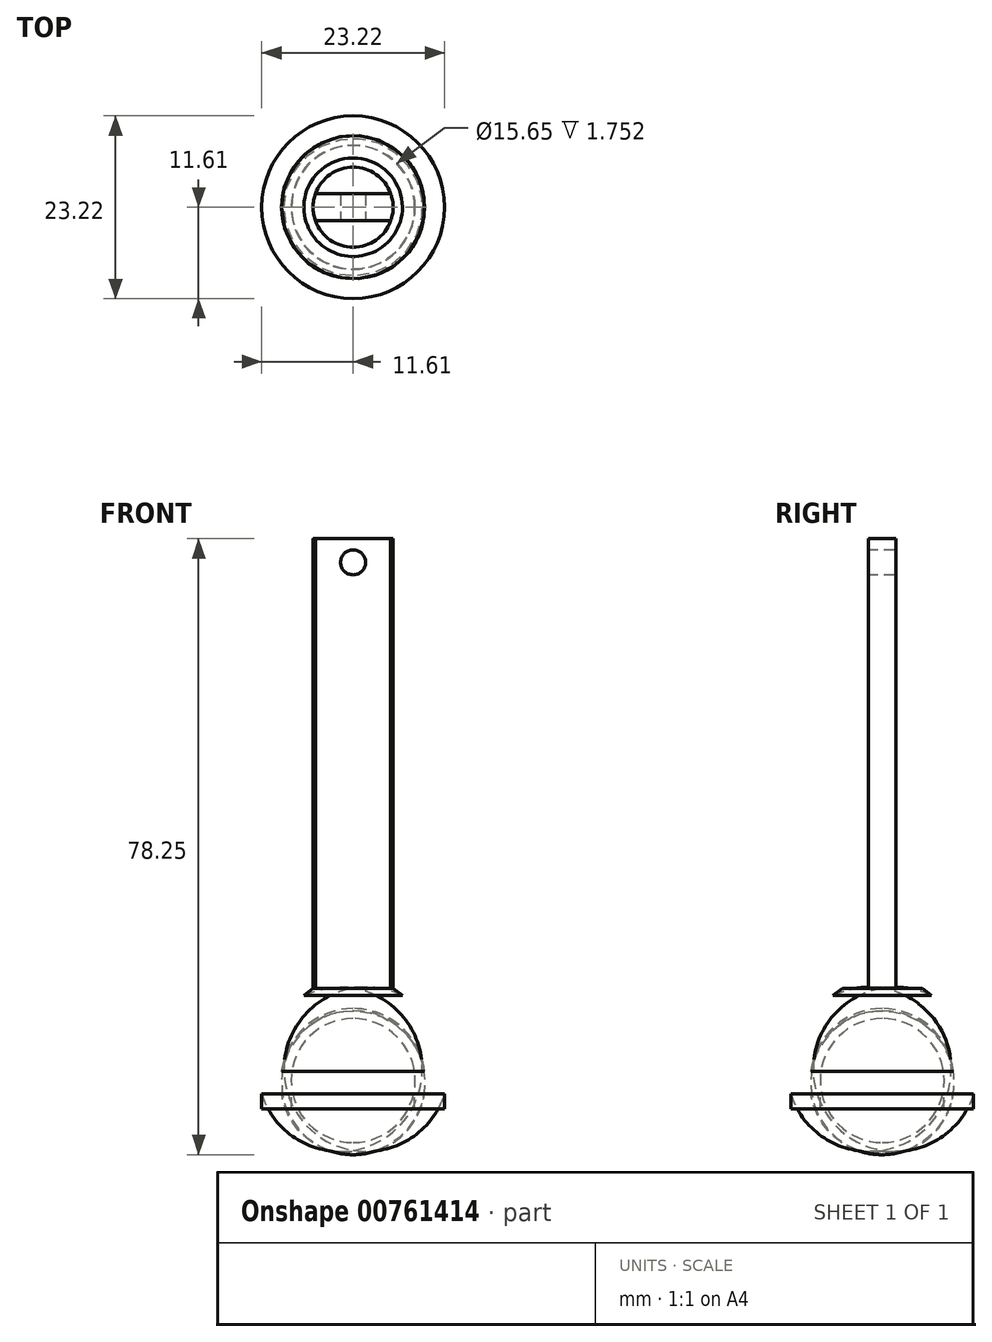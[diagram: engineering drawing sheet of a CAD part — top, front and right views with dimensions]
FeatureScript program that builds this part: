
annotation { "Feature Type Name" : "Feature", "Feature Type Description" : "" }
export const myFeature = defineFeature(function(context is Context, id is Id, definition is map)
    precondition{}
    {
        {
            var Q0;
            Q0=qCreatedBy(makeId("Front.planeOp"),FACE);
            var sketch = newSketch(context, id + "F0", { "sketchPlane" : qUnion([Q0])});
            skArc(sketch, "E0", {"start": v(0, -7.87) * mm, "mid": v(7.87, 0) * mm, "end": v(0, 7.87) * mm});
            skLineSegment(sketch, "E1", {"start": v(0, 7.87) * mm, "end": v(0, -7.87) * mm});
            skArc(sketch, "E2", {"start": v(9.07, 1.17) * mm, "mid": v(6.04, 6.87) * mm, "end": v(0, 9.14) * mm});
            skArc(sketch, "E3", {"start": v(9.07, -1.72) * mm, "mid": v(9.18, -0.28) * mm, "end": v(9.07, 1.17) * mm});
            skLineSegment(sketch, "E4", {"start": v(9.07, -1.72) * mm, "end": v(7.98, -1.72) * mm});
            skLineSegment(sketch, "E5", {"start": v(7.83, -1.88) * mm, "end": v(7.83, -3.63) * mm});
            skLineSegment(sketch, "E6", {"start": v(7.83, -3.63) * mm, "end": v(9.07, -3.63) * mm});
            skLineSegment(sketch, "E7", {"start": v(9.07, -3.63) * mm, "end": v(11.6, -3.63) * mm});
            skLineSegment(sketch, "E8", {"start": v(11.6, -3.63) * mm, "end": v(11.6, -1.72) * mm});
            skLineSegment(sketch, "E9", {"start": v(0, 9.14) * mm, "end": v(0, 11.68) * mm});
            skLineSegment(sketch, "E10", {"start": v(0, 11.68) * mm, "end": v(5.08, 11.68) * mm});
            skLineSegment(sketch, "E11", {"start": v(5.08, 11.68) * mm, "end": v(6.26, 10.79) * mm});
            skPoint(sketch, "E12.visualSharp", {"position": v(7.83, -1.72) * mm});
            skArc(sketch, "E12.filletArc", {"start": v(7.98, -1.72) * mm, "mid": v(7.87, -1.77) * mm, "end": v(7.83, -1.88) * mm});
            skArc(sketch, "E13", {"start": v(11.6, -1.72) * mm, "mid": v(11.25, 5.52) * mm, "end": v(6.26, 10.79) * mm});
            skSolve(sketch);
        }
        {
            var Q0;
            Q0 = qSketchRegion(id + "F0", true);
            var Q1;
            Q1=sQuery(id+"F0.wireOp",EDGE,"E1");
            revolve(context, id + "F1", {"surfaceOperationType" : NewSurfaceOperationType.NEW, "entities" : qUnion([Q0]), "axis" : qUnion([Q1]), "revolveType" : RevolveType.FULL});
        }
        {
            var Q0;
            Q0=makeQuery(id+"F1.opRevolve","SWEPT_FACE",FACE,{"disambiguationData":[OSD([sQuery(id+"F0.wireOp",EDGE,"E10")])]});
            var sketch = newSketch(context, id + "F2", { "sketchPlane" : qUnion([Q0])});
            skLineSegment(sketch, "E14.bottom", {"start": v(4.78, -1.73) * mm, "end": v(-4.78, -1.73) * mm});
            skLineSegment(sketch, "E14.top", {"start": v(4.78, 1.73) * mm, "end": v(-4.78, 1.73) * mm});
            skPoint(sketch, "E14.middle", {"position": v(0, 0) * mm});
            skArc(sketch, "E15", {"start": v(-4.78, 1.73) * mm, "mid": v(-5.08, 0) * mm, "end": v(-4.78, -1.73) * mm});
            skArc(sketch, "E16.trimOffspring", {"start": v(4.78, -1.73) * mm, "mid": v(5.08, 0) * mm, "end": v(4.78, 1.73) * mm});
            skSolve(sketch);
        }
        {
            var Q0;
            Q0 = qSketchRegion(id + "F2", true);
            extrude(context, id + "F3", {"entities" : qUnion([Q0]), "operationType" : NewBodyOperationType.ADD, "depth" : 57.15 * mm, "offsetDistance" : 25.4 * mm});
        }
        {
            var Q0;
            Q0=makeQuery(id+"F3.opExtrude","SWEPT_FACE",FACE,{"disambiguationData":[OSD([sQuery(id+"F2.wireOp",EDGE,"E14.bottom")])]});
            var sketch = newSketch(context, id + "F4", { "sketchPlane" : qUnion([Q0])});
            skCircle(sketch, "E17", {"center": v(0, 65.83) * mm, "radius": 1.59 * mm});
            skSolve(sketch);
        }
        {
            var Q0;
            Q0=makeQuery(id+"F4.imprint","IMPRINT",FACE,{"disambiguationData":[TD([[makeQuery(id+"F4.imprint","IMPRINT",EDGE,{"derivedFrom":sQuery(id+"F4.wireOp",EDGE,"E17")}),1.0]])]});
            extrude(context, id + "F5", {"entities" : qUnion([Q0]), "operationType" : NewBodyOperationType.REMOVE, "endBound" : BoundingType.THROUGH_ALL, "oppositeDirection" : true, "depth" : 25.4 * mm, "offsetDistance" : 25.4 * mm});
        }
    });
